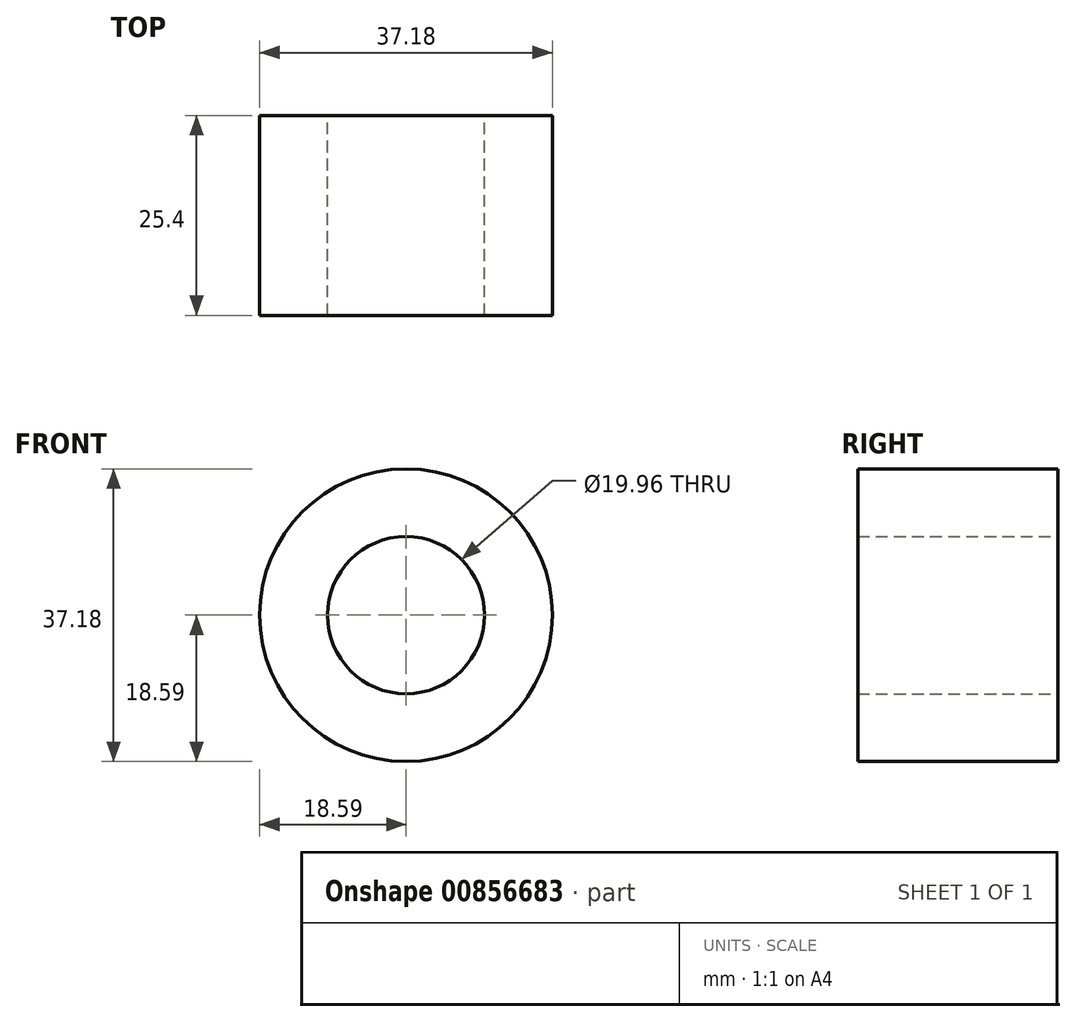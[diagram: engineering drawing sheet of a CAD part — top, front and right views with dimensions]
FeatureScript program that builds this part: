
annotation { "Feature Type Name" : "Feature", "Feature Type Description" : "" }
export const myFeature = defineFeature(function(context is Context, id is Id, definition is map)
    precondition{}
    {
        {
            var Q0;
            Q0=qCreatedBy(makeId("Front.planeOp"),FACE);
            var sketch = newSketch(context, id + "F0", { "sketchPlane" : qUnion([Q0])});
            skCircle(sketch, "E0", {"center": v(0, 0) * mm, "radius": 18.6 * mm});
            skCircle(sketch, "E1", {"center": v(0, 0) * mm, "radius": 9.98 * mm});
            skSolve(sketch);
        }
        {
            var Q0;
            Q0=makeQuery(id+"F0.imprint","IMPRINT",FACE,{"disambiguationData":[TD([[makeQuery(id+"F0.imprint","IMPRINT",EDGE,{"derivedFrom":sQuery(id+"F0.wireOp",EDGE,"E0")}),1.0]])]});
            extrude(context, id + "F1", {"entities" : qUnion([Q0]), "depth" : 25.4 * mm, "offsetDistance" : 25.4 * mm});
        }
    });
